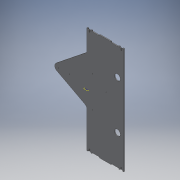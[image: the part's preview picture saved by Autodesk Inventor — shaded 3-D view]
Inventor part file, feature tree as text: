
AUTODESK INVENTOR PART (.ipt)
format: ipt  version: 2019 (Build 230136000, 136)  size: 316,928 bytes
history: native  units: in
note: dims shown in document units (in); Inventor stores cm internally (conversion verified against a paired STEP export)
features: reference x10, extrude x8, sketch x8, other x5, projected_geometry x4, fillet x2, plane x1, mirror x1, helix x1
ambient origin geometry x8: Origin, YZ Plane, XZ Plane, XY Plane, X Axis, Y Axis, Z Axis, Center Point
bodies: Solid1 (feature_tree)
feature tree (40):
  extrude  "Extrusion1"  Depth=0.1575in TaperAngle=0.0deg
  extrude  "Extrusion2"  Depth=0.1575in TaperAngle=0.0deg
  extrude  "Extrusion4"  Depth=2.5in
  extrude  "Extrusion5"  Depth=0.0394in
  plane  "Work Plane1"
  mirror  "Mirror1"
  sketch  "Sketch7"  dims[d15=1.5748in d16=10.0in d17=0.1575in d18=0.0in]
  extrude  "Extrusion6"  Depth=0.1575in
  fillet  "Fillet1"  Radius=0.1575in
  extrude  "Extrusion7"  Depth=0.1575in TaperAngle=0.0deg
  fillet  "Fillet2"  Radius=0.1969in
  extrude  "Extrusion8"  Depth=1.0in TaperAngle=0.0deg
  extrude  "Extrusion9"  [1 undecoded]
  sketch  "Sketch2"  dims[d0=7.874in d1=0.1575in d2=0.0in]
  sketch  "Sketch3"  dims[d3=0.1575in d4=0.0in d7=0.1575in d8=0.0in]
  reference  "Reference3"
  reference  "Reference4"
  sketch  "Sketch5"  dims[d9=0.1575in d10=0.0in d11=2.5in]
  projected_geometry  "Projected Loop1"
  projected_geometry  "Projected Loop2"
  projected_geometry  "Projected Loop3"
  projected_geometry  "Projected Loop4"
  sketch  "Sketch6"  dims[d12=0.1575in d13=0.0in d14=0.0394in]
  reference  "Reference7"
  reference  "Reference8"
  reference  "Reference9"
  sketch  "Sketch8"  dims[d19=0.7874in d20=0.1575in d21=0.0in d22=0.1969in]
  reference  "Reference10"
  sketch  "Sketch9"  dims[d23=0.1969in d24=1.0in d25=0.0in]
  reference  "Reference11"
  reference  "Reference12"
  sketch  "Sketch10"
  reference  "Reference13"
  reference  "Reference14"
  other  "<userpath>\Documents\CAD Files\Helix DLP\Helix DLP.iam"
  helix  "Helix DLP.iam"  [1 undecoded]
  other  "Maker_jigsaw_template:1"
  other  "Maker_jigsaw_template:2"
  other  "Projector:1"
  other  "Projector mount side:2"
note: 2 required parameter values undecoded (feature->parameter linkage not recoverable at this tier; creation-order binding heuristic only, values carry confidence <= 0.55)
